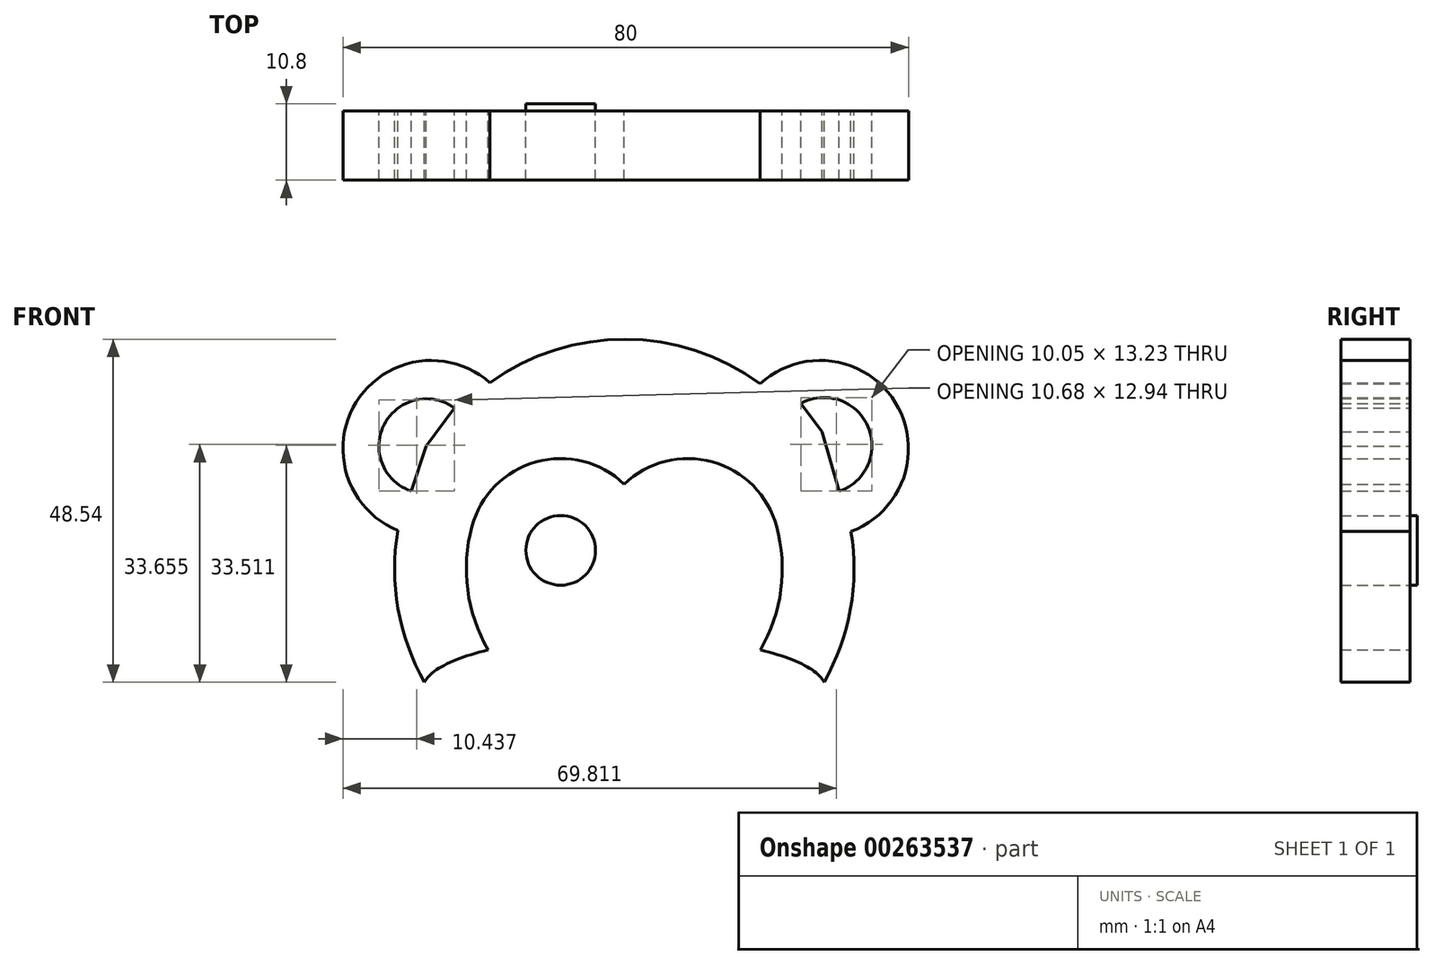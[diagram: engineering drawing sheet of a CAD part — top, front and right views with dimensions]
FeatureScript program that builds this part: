
annotation { "Feature Type Name" : "Feature", "Feature Type Description" : "" }
export const myFeature = defineFeature(function(context is Context, id is Id, definition is map)
    precondition{}
    {
        {
            var Q0;
            Q0=qCreatedBy(makeId("Front.planeOp"),FACE);
            var sketch = newSketch(context, id + "F0", { "sketchPlane" : qUnion([Q0])});
            skArc(sketch, "E0", {"start": v(28.27, -16.04) * mm, "mid": v(32, -5.7) * mm, "end": v(32.07, 5.29) * mm});
            skArc(sketch, "E1", {"start": v(-19.01, 26.36) * mm, "mid": v(-37.91, 23.6) * mm, "end": v(-32.04, 5.43) * mm});
            skArc(sketch, "E2", {"start": v(32.07, 5.29) * mm, "mid": v(38.35, 23.54) * mm, "end": v(19.23, 26.2) * mm});
            skEllipse(sketch, "E3", {"center": v(0, -17) * mm, "majorRadius": 28.5 * mm, "minorRadius": 7.5 * mm, "majorAxis": v(-1, 0)});
            skArc(sketch, "E4.trimOffspring", {"start": v(19.23, 26.2) * mm, "mid": v(0.14, 32.5) * mm, "end": v(-19.01, 26.36) * mm});
            skArc(sketch, "E5.trimOffspring", {"start": v(-32.04, 5.43) * mm, "mid": v(-32, -5.63) * mm, "end": v(-28.27, -16.04) * mm});
            skSolve(sketch);
        }
        {
            var Q0;
            {var subQ0=sQuery(id+"F0.wireOp",EDGE,"E3");var subQ1=makeQuery(id+"F0.imprint","INTERSECT",VERTEX,{"derivedFrom":[sQuery(id+"F0.wireOp",EDGE,"E0"),subQ0]});Q0=makeQuery(id+"F0.imprint","IMPRINT",FACE,{"disambiguationData":[TD([[makeQuery(id+"F0.imprint","IMPRINT",EDGE,{"disambiguationData":[TD([[subQ1,-1.0]])],"derivedFrom":subQ0}),1.0]])]});}
            var Q1;
            {var subQ1=sQuery(id+"F0.wireOp",EDGE,"E0");Q1=makeQuery(id+"F0.imprint","IMPRINT",FACE,{"disambiguationData":[TD([[makeQuery(id+"F0.imprint","IMPRINT",EDGE,{"derivedFrom":subQ1}),1.0]])]});}
            extrude(context, id + "F1", {"entities" : qUnion([Q0, Q1]), "depth" : 9.8 * mm});
        }
        {
            var Q0;
            {var subQ0=sQuery(id+"F0.wireOp",EDGE,"E3");var subQ1=makeQuery(id+"F0.imprint","INTERSECT",VERTEX,{"derivedFrom":[sQuery(id+"F0.wireOp",EDGE,"E0"),subQ0]});Q0=makeQuery(id+"F0.imprint","IMPRINT",FACE,{"disambiguationData":[TD([[makeQuery(id+"F0.imprint","IMPRINT",EDGE,{"disambiguationData":[TD([[subQ1,-1.0]])],"derivedFrom":subQ0}),1.0]])]});}
            extrude(context, id + "F2", {"entities" : qUnion([Q0]), "operationType" : NewBodyOperationType.ADD, "oppositeDirection" : true, "depth" : 1 * mm});
        }
        {
            var Q0;
            {var subQ1=sQuery(id+"F0.wireOp",EDGE,"E0");Q0=makeQuery(id+"F0.imprint","IMPRINT",FACE,{"disambiguationData":[TD([[makeQuery(id+"F0.imprint","IMPRINT",EDGE,{"derivedFrom":subQ1}),1.0]])]});}
            var sketch = newSketch(context, id + "F3", { "sketchPlane" : qUnion([Q0])});
            skArc(sketch, "E6", {"start": v(19.27, -11.47) * mm, "mid": v(22.15, -2.96) * mm, "end": v(21.55, 6) * mm});
            skArc(sketch, "E7", {"start": v(21.55, 6) * mm, "mid": v(12.49, 15.14) * mm, "end": v(0, 12) * mm});
            skArc(sketch, "E8.MirrorCS", {"start": v(-21.55, 6) * mm, "mid": v(-12.49, 15.14) * mm, "end": v(0, 12) * mm});
            skArc(sketch, "E9.MirrorCS", {"start": v(-19.27, -11.47) * mm, "mid": v(-22.15, -2.96) * mm, "end": v(-21.55, 6) * mm});
            skSolve(sketch);
        }
        {
            var Q0;
            {var subQ1=sQuery(id+"F3.wireOp",EDGE,"E6");Q0=makeQuery(id+"F3.imprint","IMPRINT",FACE,{"disambiguationData":[TD([[makeQuery(id+"F3.imprint","IMPRINT",EDGE,{"derivedFrom":subQ1}),1.0]])]});}
            extrude(context, id + "F4", {"entities" : qUnion([Q0]), "operationType" : NewBodyOperationType.ADD, "oppositeDirection" : true, "depth" : 1 * mm});
        }
        {
            var Q0;
            {var subQ0=sQuery(id+"F0.wireOp",EDGE,"E3");Q0=makeQuery(id+"F4.boolean.opBoolean","MERGE",FACE,{"derivedFrom":[makeQuery(id+"F2.opExtrude","CAP_FACE",FACE,{"disambiguationData":[OSD([subQ0])],"isStart":false}),makeQuery(id+"F4.opExtrude","CAP_FACE",FACE,{"disambiguationData":[OSD([subQ0,sQuery(id+"F3.wireOp",EDGE,"E6"),sQuery(id+"F3.wireOp",EDGE,"E7"),sQuery(id+"F3.wireOp",EDGE,"E8.MirrorCS"),sQuery(id+"F3.wireOp",EDGE,"E9.MirrorCS")])],"isStart":false})]});}
            var sketch = newSketch(context, id + "F5", { "sketchPlane" : qUnion([Q0])});
            skCircle(sketch, "E10", {"center": v(-9, 2.62) * mm, "radius": 4.93 * mm});
            skCircle(sketch, "E11.MirrorC", {"center": v(9, 2.62) * mm, "radius": 4.93 * mm});
            skSolve(sketch);
        }
        {
            var Q0;
            {var subQ5=sQuery(id+"F3.wireOp",EDGE,"E6");Q0=makeQuery(id+"F3.imprint","IMPRINT",FACE,{"disambiguationData":[TD([[makeQuery(id+"F3.imprint","IMPRINT",EDGE,{"derivedFrom":subQ5}),-1.0]])]});}
            var sketch = newSketch(context, id + "F6", { "sketchPlane" : qUnion([Q0])});
            skLineSegment(sketch, "E12", {"start": v(30.41, 11) * mm, "end": v(28, 19.4) * mm});
            skLineSegment(sketch, "E13", {"start": v(28, 19.4) * mm, "end": v(24.99, 23.43) * mm});
            skArc(sketch, "E14", {"start": v(-24.02, 22.77) * mm, "mid": v(-33.96, 20.45) * mm, "end": v(-30.11, 11) * mm});
            skLineSegment(sketch, "E15", {"start": v(-24.02, 22.77) * mm, "end": v(-28, 17.37) * mm});
            skLineSegment(sketch, "E16", {"start": v(-28, 17.37) * mm, "end": v(-30.11, 11) * mm});
            skArc(sketch, "E17", {"start": v(30.41, 11) * mm, "mid": v(34.47, 20.17) * mm, "end": v(24.99, 23.43) * mm});
            skSolve(sketch);
        }
        {
            var Q0;
            Q0=makeQuery(id+"F5.imprint","IMPRINT",FACE,{"disambiguationData":[TD([[makeQuery(id+"F5.imprint","IMPRINT",EDGE,{"derivedFrom":sQuery(id+"F5.wireOp",EDGE,"E10")}),1.0]])]});
            var Q1;
            Q1=makeQuery(id+"F5.imprint","IMPRINT",FACE,{"disambiguationData":[TD([[makeQuery(id+"F5.imprint","IMPRINT",EDGE,{"derivedFrom":sQuery(id+"F5.wireOp",EDGE,"E11.MirrorC")}),-1.0]])]});
            extrude(context, id + "F7", {"entities" : qUnion([Q0, Q1]), "operationType" : NewBodyOperationType.REMOVE, "oppositeDirection" : true, "depth" : 25 * mm});
        }
        {
            var Q0;
            Q0=makeQuery(id+"F6.imprint","IMPRINT",FACE,{"disambiguationData":[TD([[makeQuery(id+"F6.imprint","IMPRINT",EDGE,{"derivedFrom":sQuery(id+"F6.wireOp",EDGE,"E12")}),-1.0]])]});
            var Q1;
            Q1=makeQuery(id+"F6.imprint","IMPRINT",FACE,{"disambiguationData":[TD([[makeQuery(id+"F6.imprint","IMPRINT",EDGE,{"derivedFrom":sQuery(id+"F6.wireOp",EDGE,"E14")}),1.0]])]});
            extrude(context, id + "F8", {"entities" : qUnion([Q0, Q1]), "operationType" : NewBodyOperationType.REMOVE, "endBound" : BoundingType.THROUGH_ALL, "depth" : 15.9 * mm});
        }
        {
            var Q0;
            Q0=makeQuery(id+"F5.imprint","IMPRINT",FACE,{"disambiguationData":[TD([[makeQuery(id+"F5.imprint","IMPRINT",EDGE,{"derivedFrom":sQuery(id+"F5.wireOp",EDGE,"E10")}),-1.0]])]});
            extrude(context, id + "F9", {"entities" : qUnion([Q0]), "operationType" : NewBodyOperationType.REMOVE, "oppositeDirection" : true, "depth" : 2.2 * mm});
        }
        {
            var Q0;
            Q0=makeQuery(id+"F5.imprint","IMPRINT",FACE,{"disambiguationData":[TD([[makeQuery(id+"F5.imprint","IMPRINT",EDGE,{"derivedFrom":sQuery(id+"F5.wireOp",EDGE,"E10")}),-1.0]])]});
            var sketch = newSketch(context, id + "F10", { "sketchPlane" : qUnion([Q0])});
            skCircle(sketch, "E18", {"center": v(0, -6) * mm, "radius": 2 * mm});
            skSolve(sketch);
        }
        {
            var Q0;
            Q0=makeQuery(id+"F10.imprint","IMPRINT",FACE,{"disambiguationData":[TD([[makeQuery(id+"F10.imprint","IMPRINT",EDGE,{"derivedFrom":sQuery(id+"F10.wireOp",EDGE,"E18")}),1.0]])]});
            var Q1;
            Q1=sQuery(id+"F10.wireOp",EDGE,"E18");
            extrude(context, id + "F11", {"entities" : qUnion([Q0]), "operationType" : NewBodyOperationType.REMOVE, "surfaceEntities" : qUnion([Q1]), "endBound" : BoundingType.THROUGH_ALL, "oppositeDirection" : true, "depth" : 25 * mm});
        }
    });
